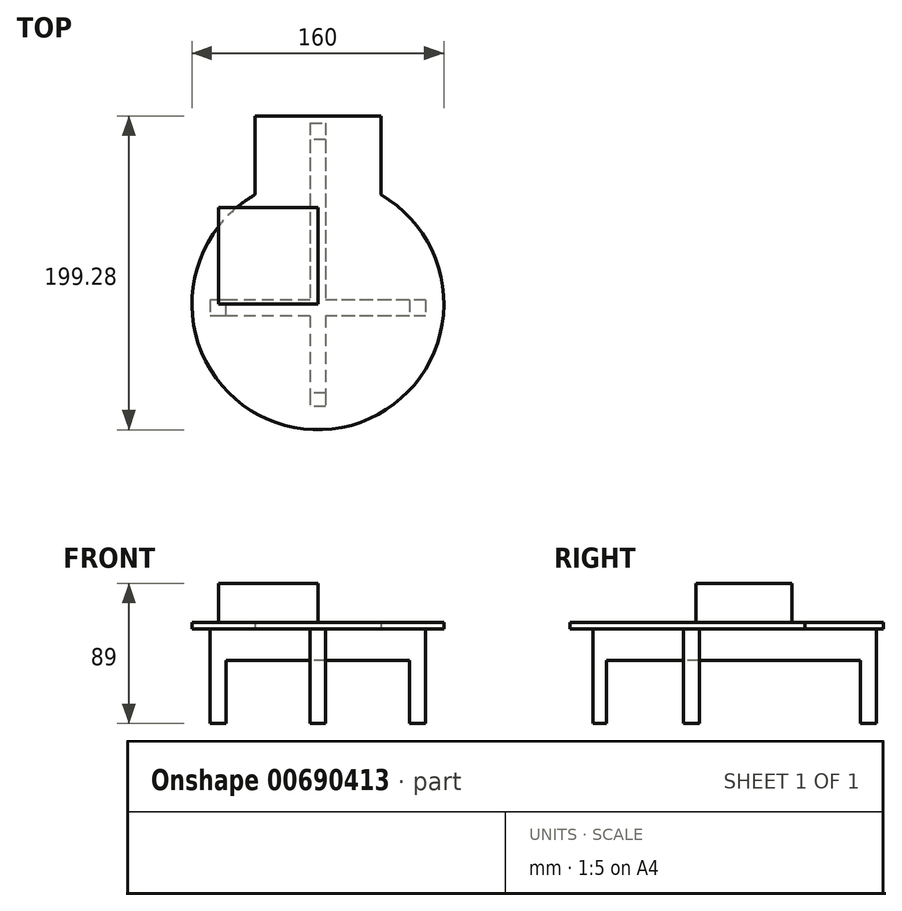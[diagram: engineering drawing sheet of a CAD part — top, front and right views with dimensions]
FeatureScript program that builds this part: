
annotation { "Feature Type Name" : "Feature", "Feature Type Description" : "" }
export const myFeature = defineFeature(function(context is Context, id is Id, definition is map)
    precondition{}
    {
        {
            var Q0;
            Q0=qCreatedBy(makeId("Top.planeOp"),FACE);
            var sketch = newSketch(context, id + "F0", { "sketchPlane" : qUnion([Q0])});
            skArc(sketch, "E0", {"start": v(-40, 69.28) * mm, "mid": v(0, -80) * mm, "end": v(40, 69.28) * mm});
            skLineSegment(sketch, "E1", {"start": v(0, 0) * mm, "end": v(-40, 0) * mm, "construction": true});
            skLineSegment(sketch, "E2", {"start": v(-40, 0) * mm, "end": v(40, 0) * mm, "construction": true});
            skLineSegment(sketch, "E3", {"start": v(-40, 0) * mm, "end": v(-40, 69.28) * mm, "construction": true});
            skLineSegment(sketch, "E4", {"start": v(40, 0) * mm, "end": v(40, 69.28) * mm, "construction": true});
            skLineSegment(sketch, "E5", {"start": v(-40, 69.28) * mm, "end": v(-40, 119.28) * mm});
            skLineSegment(sketch, "E6.MirrorCS", {"start": v(40, 69.28) * mm, "end": v(40, 119.28) * mm});
            skLineSegment(sketch, "E7", {"start": v(-40, 119.28) * mm, "end": v(40, 119.28) * mm});
            skSolve(sketch);
        }
        {
            var Q0;
            Q0=makeQuery(id+"F0.imprint","IMPRINT",FACE,{"disambiguationData":[TD([[makeQuery(id+"F0.imprint","IMPRINT",EDGE,{"derivedFrom":sQuery(id+"F0.wireOp",EDGE,"E0")}),1.0]])]});
            var sketch = newSketch(context, id + "F1", { "sketchPlane" : qUnion([Q0])});
            skSolve(sketch);
        }
        {
            var Q0;
            Q0 = qSketchRegion(id + "F0", true);
            extrude(context, id + "F2", {"entities" : qUnion([Q0]), "depth" : 4 * mm, "offsetDistance" : 25 * mm});
        }
        {
            var Q0;
            Q0=makeQuery(id+"F1.imprint","IMPRINT",FACE,{"disambiguationData":[TD([[makeQuery(id+"F1.imprint","IMPRINT",EDGE,{"derivedFrom":makeQuery(id+"F0.imprint","IMPRINT",EDGE,{"derivedFrom":sQuery(id+"F0.wireOp",EDGE,"E0")})}),1.0]])]});
            var sketch = newSketch(context, id + "F3", { "sketchPlane" : qUnion([Q0])});
            skLineSegment(sketch, "E8", {"start": v(0, 0) * mm, "end": v(0, -102.64) * mm, "construction": true});
            skLineSegment(sketch, "E9", {"start": v(0, -102.64) * mm, "end": v(0, 162.68) * mm, "construction": true});
            skLineSegment(sketch, "E10", {"start": v(0, 114.81) * mm, "end": v(5, 114.81) * mm});
            skLineSegment(sketch, "E11", {"start": v(5, 114.81) * mm, "end": v(5, -65.19) * mm});
            skLineSegment(sketch, "E12", {"start": v(5, -65.19) * mm, "end": v(0, -65.19) * mm});
            skLineSegment(sketch, "E13.MirrorCS", {"start": v(-5, 114.81) * mm, "end": v(-5, -65.19) * mm});
            skLineSegment(sketch, "E14.MirrorCS", {"start": v(-5, -65.19) * mm, "end": v(0, -65.19) * mm});
            skLineSegment(sketch, "E15.MirrorCS", {"start": v(0, 114.81) * mm, "end": v(-5, 114.81) * mm});
            skLineSegment(sketch, "E16.bottom", {"start": v(68.52, 2.35) * mm, "end": v(-68.48, 2.35) * mm});
            skLineSegment(sketch, "E16.top", {"start": v(68.52, -7.65) * mm, "end": v(-68.48, -7.65) * mm});
            skLineSegment(sketch, "E16.left", {"start": v(68.52, 2.35) * mm, "end": v(68.52, -7.65) * mm});
            skLineSegment(sketch, "E16.right", {"start": v(-68.48, 2.35) * mm, "end": v(-68.48, -7.65) * mm});
            skSolve(sketch);
        }
        {
            var Q0;
            Q0 = qSketchRegion(id + "F3", true);
            extrude(context, id + "F4", {"entities" : qUnion([Q0]), "operationType" : NewBodyOperationType.ADD, "oppositeDirection" : true, "depth" : 20 * mm, "offsetDistance" : 25 * mm});
        }
        {
            var Q0;
            Q0=makeQuery(id+"F4.opExtrude","CAP_FACE",FACE,{"disambiguationData":[OSD([sQuery(id+"F3.wireOp",EDGE,"E10"),sQuery(id+"F3.wireOp",EDGE,"E11"),sQuery(id+"F3.wireOp",EDGE,"E12"),sQuery(id+"F3.wireOp",EDGE,"E13.MirrorCS"),sQuery(id+"F3.wireOp",EDGE,"E14.MirrorCS"),sQuery(id+"F3.wireOp",EDGE,"E15.MirrorCS"),sQuery(id+"F3.wireOp",EDGE,"E16.bottom"),sQuery(id+"F3.wireOp",EDGE,"E16.top"),sQuery(id+"F3.wireOp",EDGE,"E16.left"),sQuery(id+"F3.wireOp",EDGE,"E16.right")])],"isStart":false});
            var sketch = newSketch(context, id + "F5", { "sketchPlane" : qUnion([Q0])});
            skLineSegment(sketch, "E17.bottom", {"start": v(68.52, -2.35) * mm, "end": v(58.16, -2.35) * mm});
            skLineSegment(sketch, "E17.top", {"start": v(68.52, 7.65) * mm, "end": v(58.16, 7.65) * mm});
            skLineSegment(sketch, "E17.left", {"start": v(68.52, -2.35) * mm, "end": v(68.52, 7.65) * mm});
            skLineSegment(sketch, "E17.right", {"start": v(58.16, -2.35) * mm, "end": v(58.16, 7.65) * mm});
            skLineSegment(sketch, "E18.bottom", {"start": v(-68.48, 7.65) * mm, "end": v(-58.23, 7.65) * mm});
            skLineSegment(sketch, "E18.top", {"start": v(-68.48, -2.35) * mm, "end": v(-58.23, -2.35) * mm});
            skLineSegment(sketch, "E18.left", {"start": v(-68.48, 7.65) * mm, "end": v(-68.48, -2.35) * mm});
            skLineSegment(sketch, "E18.right", {"start": v(-58.23, 7.65) * mm, "end": v(-58.23, -2.35) * mm});
            skLineSegment(sketch, "E19.bottom", {"start": v(5, 65.19) * mm, "end": v(-5, 65.19) * mm});
            skLineSegment(sketch, "E19.top", {"start": v(5, 56.64) * mm, "end": v(-5, 56.64) * mm});
            skLineSegment(sketch, "E19.left", {"start": v(5, 65.19) * mm, "end": v(5, 56.64) * mm});
            skLineSegment(sketch, "E19.right", {"start": v(-5, 65.19) * mm, "end": v(-5, 56.64) * mm});
            skLineSegment(sketch, "E20.bottom", {"start": v(5, -114.81) * mm, "end": v(-5, -114.81) * mm});
            skLineSegment(sketch, "E20.top", {"start": v(5, -104.44) * mm, "end": v(-5, -104.44) * mm});
            skLineSegment(sketch, "E20.left", {"start": v(5, -114.81) * mm, "end": v(5, -104.44) * mm});
            skLineSegment(sketch, "E20.right", {"start": v(-5, -114.81) * mm, "end": v(-5, -104.44) * mm});
            skSolve(sketch);
        }
        {
            var Q0;
            Q0 = qSketchRegion(id + "F5", true);
            extrude(context, id + "F6", {"entities" : qUnion([Q0]), "operationType" : NewBodyOperationType.ADD, "depth" : 40 * mm, "offsetDistance" : 25 * mm});
        }
        {
            var Q0;
            Q0=makeQuery(id+"F2.opExtrude","CAP_FACE",FACE,{"disambiguationData":[OSD([sQuery(id+"F0.wireOp",EDGE,"E0"),sQuery(id+"F0.wireOp",EDGE,"E5"),sQuery(id+"F0.wireOp",EDGE,"E6.MirrorCS"),sQuery(id+"F0.wireOp",EDGE,"E7")])],"isStart":false});
            var sketch = newSketch(context, id + "F7", { "sketchPlane" : qUnion([Q0])});
            skLineSegment(sketch, "E21.bottom", {"start": v(0, 61.18) * mm, "end": v(-63.04, 61.18) * mm});
            skLineSegment(sketch, "E21.top", {"start": v(0, 0) * mm, "end": v(-63.04, 0) * mm});
            skLineSegment(sketch, "E21.left", {"start": v(0, 61.18) * mm, "end": v(0, 0) * mm});
            skLineSegment(sketch, "E21.right", {"start": v(-63.04, 61.18) * mm, "end": v(-63.04, 0) * mm});
            skSolve(sketch);
        }
        {
            var Q0;
            Q0 = qSketchRegion(id + "F7", true);
            extrude(context, id + "F8", {"entities" : qUnion([Q0]), "operationType" : NewBodyOperationType.ADD, "depth" : 25 * mm, "offsetDistance" : 25 * mm});
        }
    });
